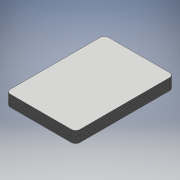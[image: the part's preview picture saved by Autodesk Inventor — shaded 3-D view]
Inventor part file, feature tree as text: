
AUTODESK INVENTOR PART (.ipt)
format: ipt  version: 2018 (Build 220112000, 112)  size: 318,976 bytes
history: native  units: mm
features: extrude x1, pattern_linear x1, sketch x1
ambient origin geometry x8: Origin, YZ Plane, XZ Plane, XY Plane, X Axis, Y Axis, Z Axis, Center Point
bodies: Solid1 (feature_tree)
feature tree (3):
  extrude  "Extrusion1"  Depth=89.0mm
  pattern_linear  "Rectangular Pattern1"  Spacing1=4.0mm  [1 undecoded]
  sketch  "Sketch1"  dims[d0=63.0mm d1=89.0mm d2=4.0mm d3=0.27mm d4=0.0mm d5=370.0mm d7=10.03mm]
note: 1 required parameter value undecoded (feature->parameter linkage not recoverable at this tier; creation-order binding heuristic only, values carry confidence <= 0.55)
